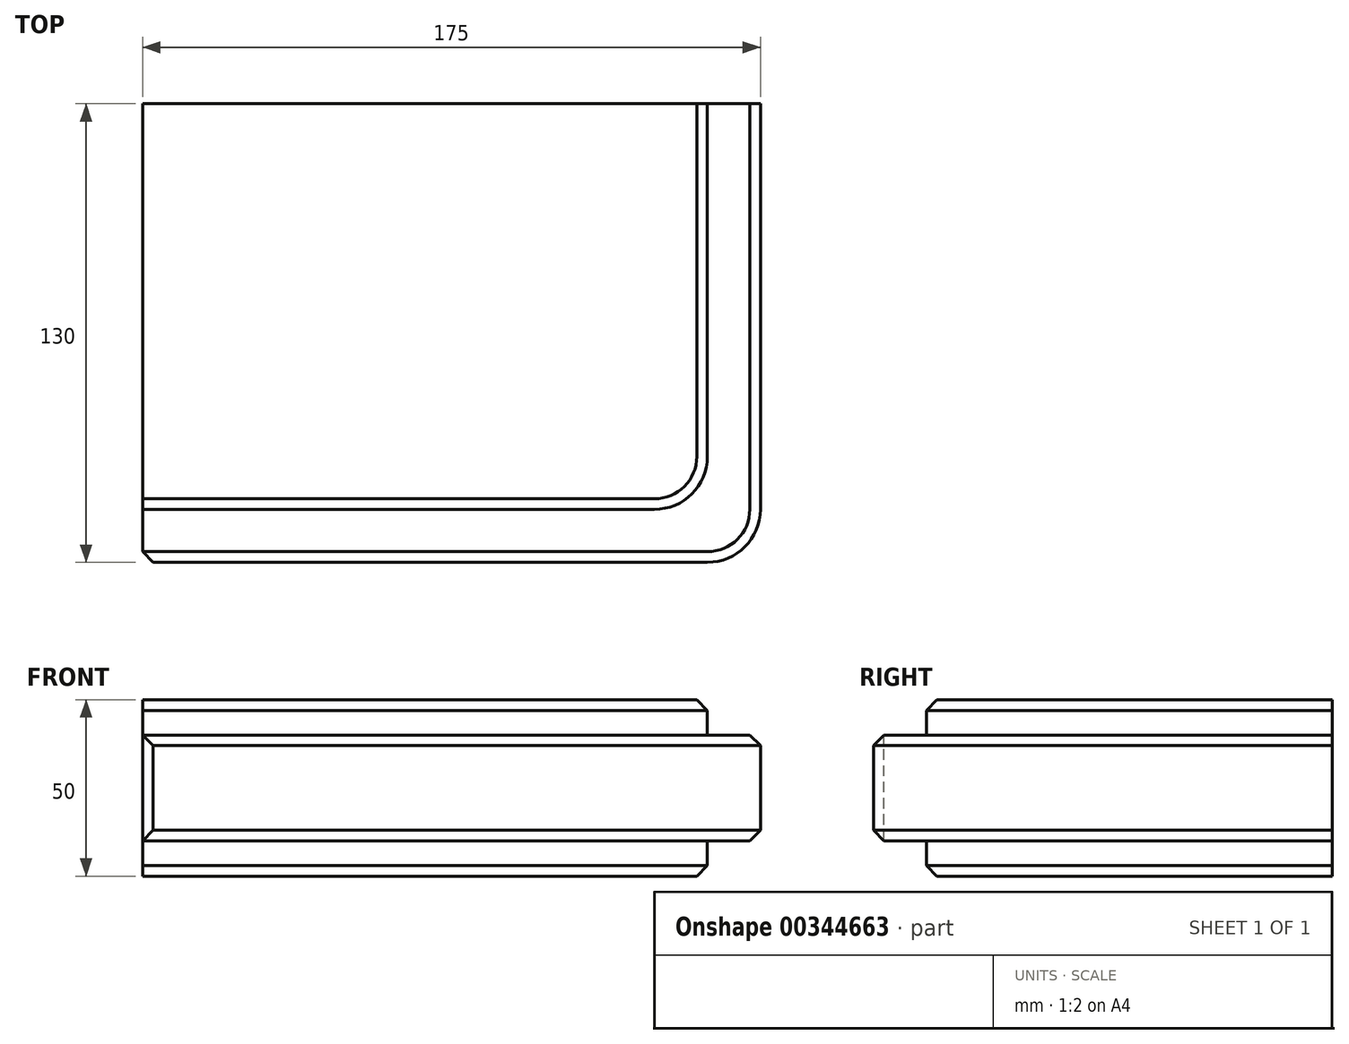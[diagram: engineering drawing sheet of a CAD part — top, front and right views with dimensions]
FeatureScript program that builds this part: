
annotation { "Feature Type Name" : "Feature", "Feature Type Description" : "" }
export const myFeature = defineFeature(function(context is Context, id is Id, definition is map)
    precondition{}
    {
        {
            var Q0;
            Q0=qCreatedBy(makeId("Top.planeOp"),FACE);
            var sketch = newSketch(context, id + "F0", { "sketchPlane" : qUnion([Q0])});
            skLineSegment(sketch, "E0.bottom", {"start": v(87.5, -65) * mm, "end": v(-87.5, -65) * mm});
            skLineSegment(sketch, "E0.top", {"start": v(87.5, 65) * mm, "end": v(-87.5, 65) * mm});
            skLineSegment(sketch, "E0.left", {"start": v(87.5, -65) * mm, "end": v(87.5, 65) * mm});
            skLineSegment(sketch, "E0.right", {"start": v(-87.5, -65) * mm, "end": v(-87.5, 65) * mm});
            skPoint(sketch, "E0.middle", {"position": v(0, 0) * mm});
            skSolve(sketch);
        }
        {
            var Q0;
            Q0 = qSketchRegion(id + "F0", true);
            extrude(context, id + "F1", {"entities" : qUnion([Q0]), "depth" : 15 * mm, "hasSecondDirection" : true, "secondDirectionOppositeDirection" : true, "secondDirectionDepth" : 15 * mm});
        }
        {
            var Q0;
            Q0=qCreatedBy(makeId("Top.planeOp"),FACE);
            var sketch = newSketch(context, id + "F2", { "sketchPlane" : qUnion([Q0])});
            skLineSegment(sketch, "E1.bottom", {"start": v(-87.5, 65) * mm, "end": v(72.5, 65) * mm});
            skLineSegment(sketch, "E1.top", {"start": v(-87.5, -50) * mm, "end": v(72.5, -50) * mm});
            skLineSegment(sketch, "E1.left", {"start": v(-87.5, 65) * mm, "end": v(-87.5, -50) * mm});
            skLineSegment(sketch, "E1.right", {"start": v(72.5, 65) * mm, "end": v(72.5, -50) * mm});
            skSolve(sketch);
        }
        {
            var Q0;
            Q0 = qSketchRegion(id + "F2", true);
            extrude(context, id + "F3", {"entities" : qUnion([Q0]), "operationType" : NewBodyOperationType.ADD, "depth" : 25 * mm, "hasSecondDirection" : true, "secondDirectionOppositeDirection" : true, "secondDirectionDepth" : 25 * mm});
        }
        {
            var Q0;
            Q0=makeQuery(id+"F1.opExtrude","SWEPT_EDGE",EDGE,{"disambiguationData":[OSD([sQuery(id+"F0.wireOp",EDGE,"E0.bottom"),sQuery(id+"F0.wireOp",EDGE,"E0.left")])]});
            var Q1;
            {var subQ0=sQuery(id+"F2.wireOp",EDGE,"E1.right");var subQ1=sQuery(id+"F2.wireOp",EDGE,"E1.top");Q1=makeQuery(id+"F3.boolean.opBoolean","SPLIT",EDGE,{"disambiguationData":[TD([makeQuery(id+"F1.opExtrude","CAP_FACE",FACE,{"disambiguationData":[OSD([sQuery(id+"F0.wireOp",EDGE,"E0.bottom"),sQuery(id+"F0.wireOp",EDGE,"E0.top"),sQuery(id+"F0.wireOp",EDGE,"E0.left"),sQuery(id+"F0.wireOp",EDGE,"E0.right")])],"isStart":false})])],"derivedFrom":makeQuery(id+"F3.opExtrude","SWEPT_EDGE",EDGE,{"disambiguationData":[OSD([subQ1,subQ0])]})});}
            var Q2;
            {var subQ0=sQuery(id+"F2.wireOp",EDGE,"E1.top");var subQ1=sQuery(id+"F2.wireOp",EDGE,"E1.right");Q2=makeQuery(id+"F3.boolean.opBoolean","SPLIT",EDGE,{"disambiguationData":[TD([makeQuery(id+"F1.opExtrude","CAP_FACE",FACE,{"disambiguationData":[OSD([sQuery(id+"F0.wireOp",EDGE,"E0.bottom"),sQuery(id+"F0.wireOp",EDGE,"E0.top"),sQuery(id+"F0.wireOp",EDGE,"E0.left"),sQuery(id+"F0.wireOp",EDGE,"E0.right")])],"isStart":true})])],"derivedFrom":makeQuery(id+"F3.opExtrude","SWEPT_EDGE",EDGE,{"disambiguationData":[OSD([subQ0,subQ1])]})});}
            fillet(context, id + "F4", {"entities" : qUnion([Q0, Q1, Q2]), "radius" : 15 * mm, "tangentPropagation" : true, "allowEdgeOverflow" : false});
        }
        {
            var Q0;
            Q0=makeQuery(id+"F3.opExtrude","CAP_EDGE",EDGE,{"disambiguationData":[OSD([sQuery(id+"F2.wireOp",EDGE,"E1.right")])],"isStart":false});
            var Q1;
            {var subQ0=sQuery(id+"F2.wireOp",EDGE,"E1.right");var subQ1=sQuery(id+"F2.wireOp",EDGE,"E1.top");var subQ2=makeQuery(id+"F3.opExtrude","CAP_FACE",FACE,{"disambiguationData":[OSD([sQuery(id+"F2.wireOp",EDGE,"E1.bottom"),subQ1,sQuery(id+"F2.wireOp",EDGE,"E1.left"),subQ0])],"isStart":false});Q1=makeQuery(id+"F4.opFillet","BLEND_EDGE",EDGE,{"blendedFrom":[makeQuery(id+"F3.boolean.opBoolean","SPLIT",EDGE,{"disambiguationData":[TD([makeQuery(id+"F1.opExtrude","CAP_FACE",FACE,{"disambiguationData":[OSD([sQuery(id+"F0.wireOp",EDGE,"E0.bottom"),sQuery(id+"F0.wireOp",EDGE,"E0.top"),sQuery(id+"F0.wireOp",EDGE,"E0.left"),sQuery(id+"F0.wireOp",EDGE,"E0.right")])],"isStart":false})])],"derivedFrom":makeQuery(id+"F3.opExtrude","SWEPT_EDGE",EDGE,{"disambiguationData":[OSD([subQ1,subQ0])]})}),subQ2],"blendedInto":[subQ2]});}
            var Q2;
            Q2=makeQuery(id+"F3.opExtrude","CAP_EDGE",EDGE,{"disambiguationData":[OSD([sQuery(id+"F2.wireOp",EDGE,"E1.top")])],"isStart":false});
            var Q3;
            Q3=makeQuery(id+"F1.opExtrude","CAP_EDGE",EDGE,{"disambiguationData":[OSD([sQuery(id+"F0.wireOp",EDGE,"E0.bottom")])],"isStart":false});
            var Q4;
            Q4=makeQuery(id+"F1.opExtrude","SWEPT_FACE",FACE,{"disambiguationData":[OSD([sQuery(id+"F0.wireOp",EDGE,"E0.bottom")])]});
            var Q5;
            Q5=makeQuery(id+"F3.opExtrude","CAP_EDGE",EDGE,{"disambiguationData":[OSD([sQuery(id+"F2.wireOp",EDGE,"E1.top")])],"isStart":true});
            var Q6;
            Q6=makeQuery(id+"F3.opExtrude","CAP_EDGE",EDGE,{"disambiguationData":[OSD([sQuery(id+"F2.wireOp",EDGE,"E1.right")])],"isStart":true});
            chamfer(context, id + "F5", {"entities" : qUnion([Q0, Q1, Q2, Q3, Q4, Q5, Q6]), "width" : 3 * mm, "tangentPropagation" : true});
        }
    });
